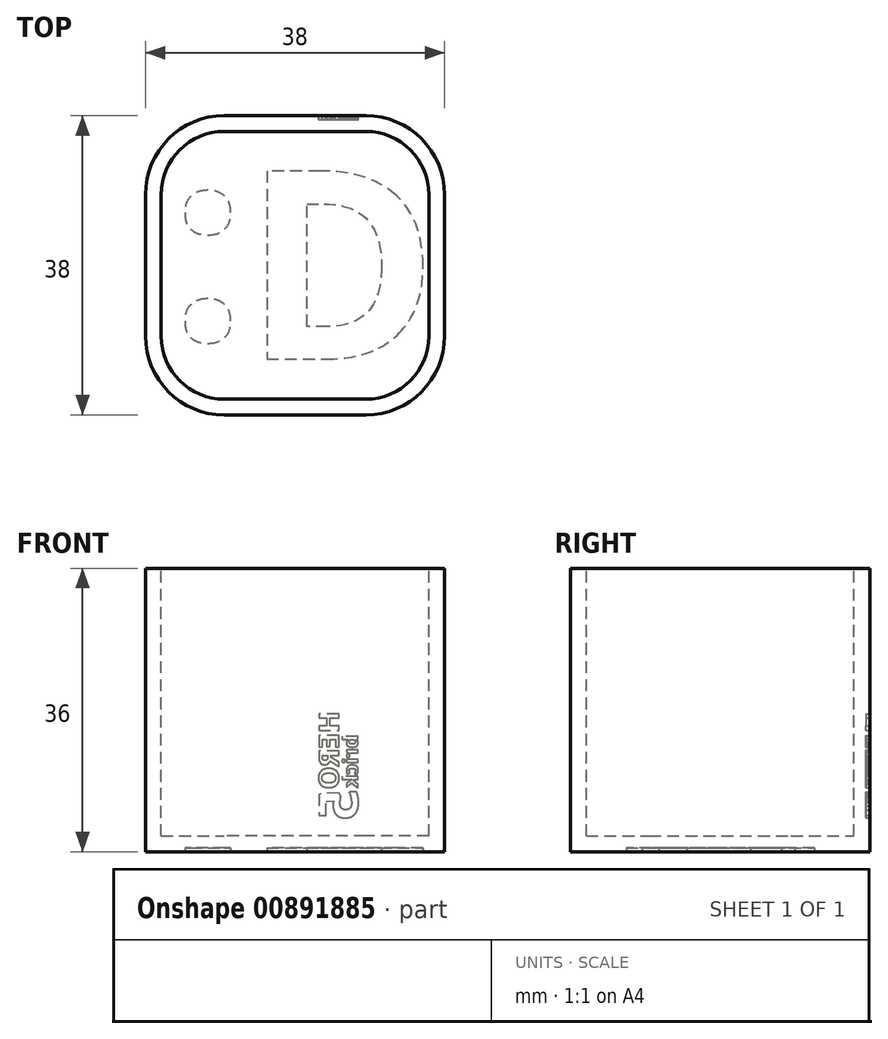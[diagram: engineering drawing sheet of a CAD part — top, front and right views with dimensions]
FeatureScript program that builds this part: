
annotation { "Feature Type Name" : "Feature", "Feature Type Description" : "" }
export const myFeature = defineFeature(function(context is Context, id is Id, definition is map)
    precondition{}
    {
        {
            var Q0;
            Q0=qCreatedBy(makeId("Top.planeOp"),FACE);
            var sketch = newSketch(context, id + "F0", { "sketchPlane" : qUnion([Q0])});
            skLineSegment(sketch, "E0.bottom", {"start": v(19, 19) * mm, "end": v(-19, 19) * mm});
            skLineSegment(sketch, "E0.top", {"start": v(19, -19) * mm, "end": v(-19, -19) * mm});
            skLineSegment(sketch, "E0.left", {"start": v(19, 19) * mm, "end": v(19, -19) * mm});
            skLineSegment(sketch, "E0.right", {"start": v(-19, 19) * mm, "end": v(-19, -19) * mm});
            skPoint(sketch, "E0.middle", {"position": v(0, 0) * mm});
            skSolve(sketch);
        }
        {
            var Q0;
            Q0 = qSketchRegion(id + "F0", true);
            extrude(context, id + "F1", {"entities" : qUnion([Q0]), "depth" : 36 * mm, "offsetDistance" : 25 * mm});
        }
        {
            var Q0;
            Q0=makeQuery(id+"F1.opExtrude","SWEPT_EDGE",EDGE,{"disambiguationData":[OSD([sQuery(id+"F0.wireOp",EDGE,"E0.top"),sQuery(id+"F0.wireOp",EDGE,"E0.right")])]});
            var Q1;
            Q1=makeQuery(id+"F1.opExtrude","SWEPT_EDGE",EDGE,{"disambiguationData":[OSD([sQuery(id+"F0.wireOp",EDGE,"E0.bottom"),sQuery(id+"F0.wireOp",EDGE,"E0.right")])]});
            var Q2;
            Q2=makeQuery(id+"F1.opExtrude","SWEPT_EDGE",EDGE,{"disambiguationData":[OSD([sQuery(id+"F0.wireOp",EDGE,"E0.bottom"),sQuery(id+"F0.wireOp",EDGE,"E0.left")])]});
            var Q3;
            Q3=makeQuery(id+"F1.opExtrude","SWEPT_EDGE",EDGE,{"disambiguationData":[OSD([sQuery(id+"F0.wireOp",EDGE,"E0.top"),sQuery(id+"F0.wireOp",EDGE,"E0.left")])]});
            fillet(context, id + "F2", {"entities" : qUnion([Q0, Q1, Q2, Q3]), "radius" : 10 * mm, "tangentPropagation" : true, "allowEdgeOverflow" : false});
        }
        {
            var Q0;
            Q0=makeQuery(id+"F1.opExtrude","CAP_FACE",FACE,{"disambiguationData":[OSD([sQuery(id+"F0.wireOp",EDGE,"E0.bottom"),sQuery(id+"F0.wireOp",EDGE,"E0.top"),sQuery(id+"F0.wireOp",EDGE,"E0.left"),sQuery(id+"F0.wireOp",EDGE,"E0.right")])],"isStart":true});
            shell(context, id + "F3", {"entities" : qUnion([Q0]), "thickness" : 2 * mm});
        }
        {
            var Q0;
            Q0=makeQuery(id+"F1.opExtrude","SWEPT_FACE",FACE,{"disambiguationData":[OSD([sQuery(id+"F0.wireOp",EDGE,"E0.top")])]});
            var sketch = newSketch(context, id + "F4", { "sketchPlane" : qUnion([Q0])});
            skText(sketch, "E1", { "text": "HERO", "fontName": "OpenSans-Bold.ttf"});
            skText(sketch, "E2", { "text": "5", "fontName": "OpenSans-Bold.ttf"});
            skText(sketch, "E3", { "text": "brick", "fontName": "OpenSans-Bold.ttf"});
            const initialGuessF4  = {"E1": [0.00556, 0.01816, 0, 1, 0.00256], "E2": [0.008, 0.02806, 0, 1, 0.005], "E3": [0.008, 0.02115, 0, 1, 0.00192]};
            skSetInitialGuess(sketch, initialGuessF4);
            skSolve(sketch);
        }
        {
            var Q0;
            Q0 = qSketchRegion(id + "F4", true);
            extrude(context, id + "F5", {"entities" : qUnion([Q0]), "operationType" : NewBodyOperationType.REMOVE, "oppositeDirection" : true, "depth" : .5 * mm, "offsetDistance" : 25 * mm});
        }
        {
            var Q0;
            Q0=makeQuery(id+"F1.opExtrude","CAP_FACE",FACE,{"disambiguationData":[OSD([sQuery(id+"F0.wireOp",EDGE,"E0.bottom"),sQuery(id+"F0.wireOp",EDGE,"E0.top"),sQuery(id+"F0.wireOp",EDGE,"E0.left"),sQuery(id+"F0.wireOp",EDGE,"E0.right")])],"isStart":false});
            var sketch = newSketch(context, id + "F6", { "sketchPlane" : qUnion([Q0])});
            skText(sketch, "E4", { "text": "D", "fontName": "NotoSans-Bold.ttf"});
            skText(sketch, "E5", { "text": ":", "fontName": "OpenSans-Bold.ttf"});
            const initialGuessF6  = {"E4": [-0.00658, -0.01198, 1, 0, 0.0241], "E5": [-0.01595, -0.00908, 1, 0, 0.02459]};
            skSetInitialGuess(sketch, initialGuessF6);
            skSolve(sketch);
        }
        {
            var Q0;
            Q0 = qSketchRegion(id + "F6", true);
            extrude(context, id + "F7", {"entities" : qUnion([Q0]), "operationType" : NewBodyOperationType.REMOVE, "oppositeDirection" : true, "depth" : .5 * mm, "offsetDistance" : 25 * mm});
        }
        {
            var Q0;
            Q0=makeQuery(id+"F1.opExtrude","SWEPT_BODY",BODY,{"disambiguationData":[OSD([sQuery(id+"F0.wireOp",EDGE,"E0.bottom"),sQuery(id+"F0.wireOp",EDGE,"E0.top"),sQuery(id+"F0.wireOp",EDGE,"E0.left"),sQuery(id+"F0.wireOp",EDGE,"E0.right")])]});
            var Q1;
            Q1=makeQuery(id+"F1.opExtrude","CAP_EDGE",EDGE,{"disambiguationData":[OSD([sQuery(id+"F0.wireOp",EDGE,"E0.top")])],"isStart":false});
            transform(context, id + "F8", {"entities" : qUnion([Q0]), "transformType" : TransformType.ROTATION, "transformAxis" : qUnion([Q1]), "angle" : 180 * degree, "makeCopy" : false});
        }
    });
